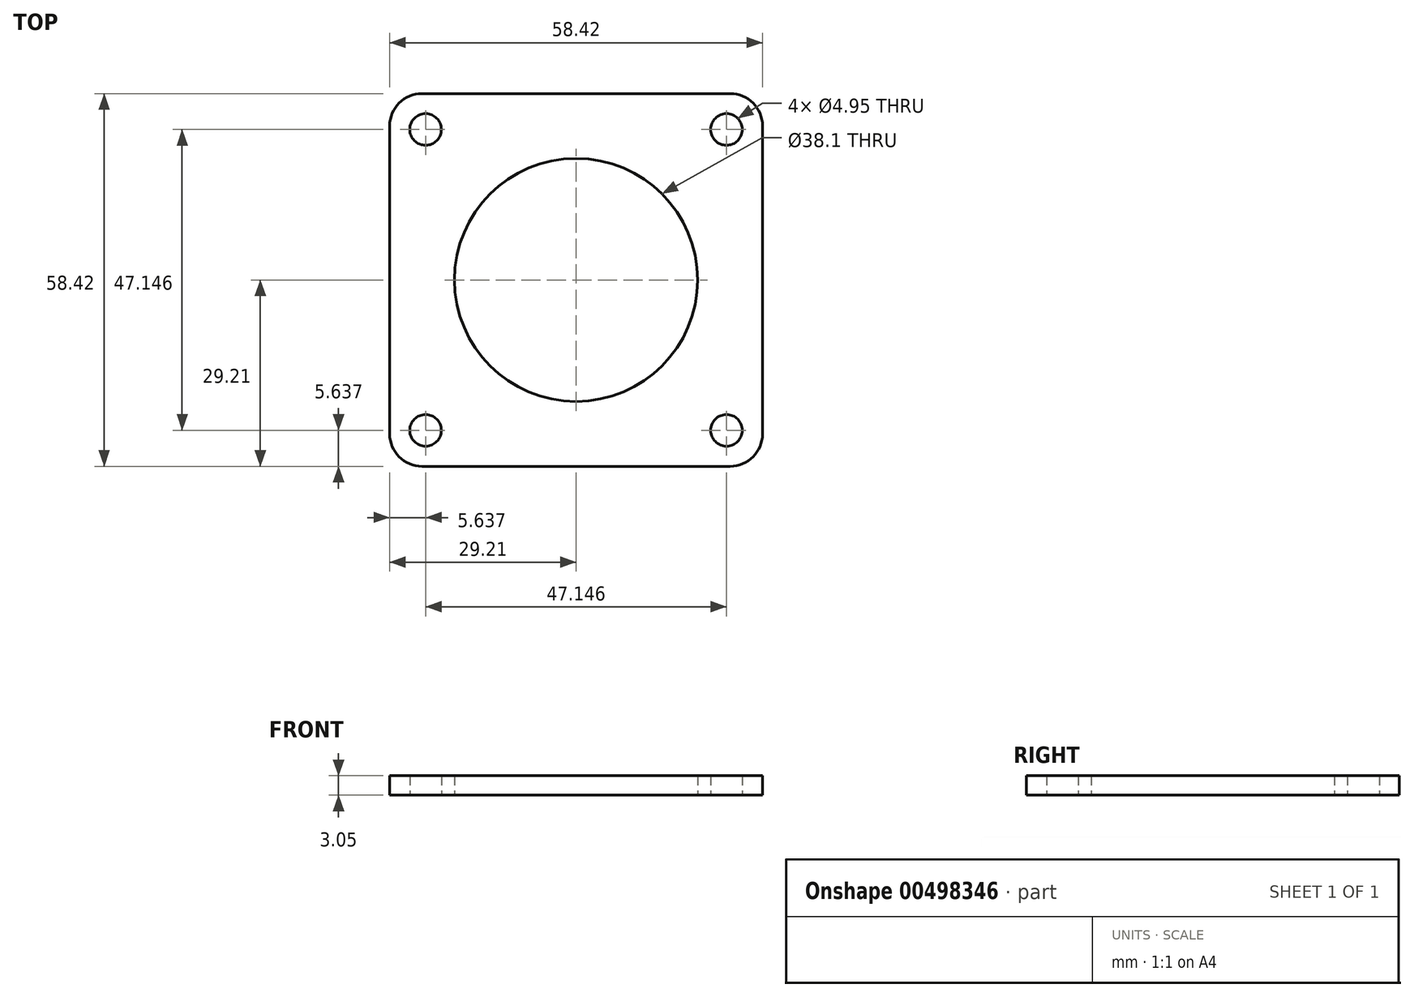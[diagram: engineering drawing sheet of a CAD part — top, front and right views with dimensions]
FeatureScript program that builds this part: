
annotation { "Feature Type Name" : "Feature", "Feature Type Description" : "" }
export const myFeature = defineFeature(function(context is Context, id is Id, definition is map)
    precondition{}
    {
        {
            var Q0;
            Q0=qCreatedBy(makeId("Top.planeOp"),FACE);
            var sketch = newSketch(context, id + "F0", { "sketchPlane" : qUnion([Q0])});
            skLineSegment(sketch, "E0.bottom", {"start": v(-29.21, 29.2) * mm, "end": v(29.2, 29.21) * mm});
            skLineSegment(sketch, "E0.top", {"start": v(-29.21, -29.21) * mm, "end": v(29.2, -29.2) * mm});
            skLineSegment(sketch, "E0.left", {"start": v(-29.21, 29.2) * mm, "end": v(-29.21, -29.21) * mm});
            skLineSegment(sketch, "E0.right", {"start": v(29.2, 29.21) * mm, "end": v(29.2, -29.2) * mm});
            skCircle(sketch, "E1", {"center": v(0, 0) * mm, "radius": 19.05 * mm});
            skCircle(sketch, "E2", {"center": v(0, 0) * mm, "radius": 33.34 * mm, "construction": true});
            skLineSegment(sketch, "E3", {"start": v(-29.2, -29.2) * mm, "end": v(29.2, 29.2) * mm, "construction": true});
            skLineSegment(sketch, "E4", {"start": v(29.21, -29.2) * mm, "end": v(-29.21, 29.21) * mm, "construction": true});
            skCircle(sketch, "E5", {"center": v(23.57, 23.57) * mm, "radius": 2.48 * mm});
            skCircle(sketch, "E6", {"center": v(-23.57, 23.57) * mm, "radius": 2.48 * mm});
            skCircle(sketch, "E7", {"center": v(-23.57, -23.57) * mm, "radius": 2.48 * mm});
            skCircle(sketch, "E8", {"center": v(23.57, -23.57) * mm, "radius": 2.48 * mm});
            skSolve(sketch);
        }
        {
            var Q0;
            Q0=makeQuery(id+"F0.imprint","IMPRINT",FACE,{"disambiguationData":[TD([[makeQuery(id+"F0.imprint","IMPRINT",EDGE,{"derivedFrom":sQuery(id+"F0.wireOp",EDGE,"E0.bottom")}),-1.0]])]});
            extrude(context, id + "F1", {"entities" : qUnion([Q0]), "depth" : 3.05 * mm});
        }
        {
            var Q0;
            Q0=makeQuery(id+"F1.opExtrude","SWEPT_EDGE",EDGE,{"disambiguationData":[OSD([sQuery(id+"F0.wireOp",EDGE,"E0.bottom"),sQuery(id+"F0.wireOp",EDGE,"E0.left")])]});
            fillet(context, id + "F2", {"entities" : qUnion([Q0]), "radius" : 5.08 * mm, "tangentPropagation" : true, "allowEdgeOverflow" : false});
        }
        {
            var Q0;
            Q0=makeQuery(id+"F1.opExtrude","SWEPT_EDGE",EDGE,{"disambiguationData":[OSD([sQuery(id+"F0.wireOp",EDGE,"E0.bottom"),sQuery(id+"F0.wireOp",EDGE,"E0.right")])]});
            var Q1;
            Q1=makeQuery(id+"F1.opExtrude","SWEPT_EDGE",EDGE,{"disambiguationData":[OSD([sQuery(id+"F0.wireOp",EDGE,"E0.top"),sQuery(id+"F0.wireOp",EDGE,"E0.right")])]});
            var Q2;
            Q2=makeQuery(id+"F1.opExtrude","SWEPT_EDGE",EDGE,{"disambiguationData":[OSD([sQuery(id+"F0.wireOp",EDGE,"E0.top"),sQuery(id+"F0.wireOp",EDGE,"E0.left")])]});
            fillet(context, id + "F3", {"entities" : qUnion([Q0, Q1, Q2]), "radius" : 5.08 * mm, "tangentPropagation" : true, "allowEdgeOverflow" : false});
        }
    });
